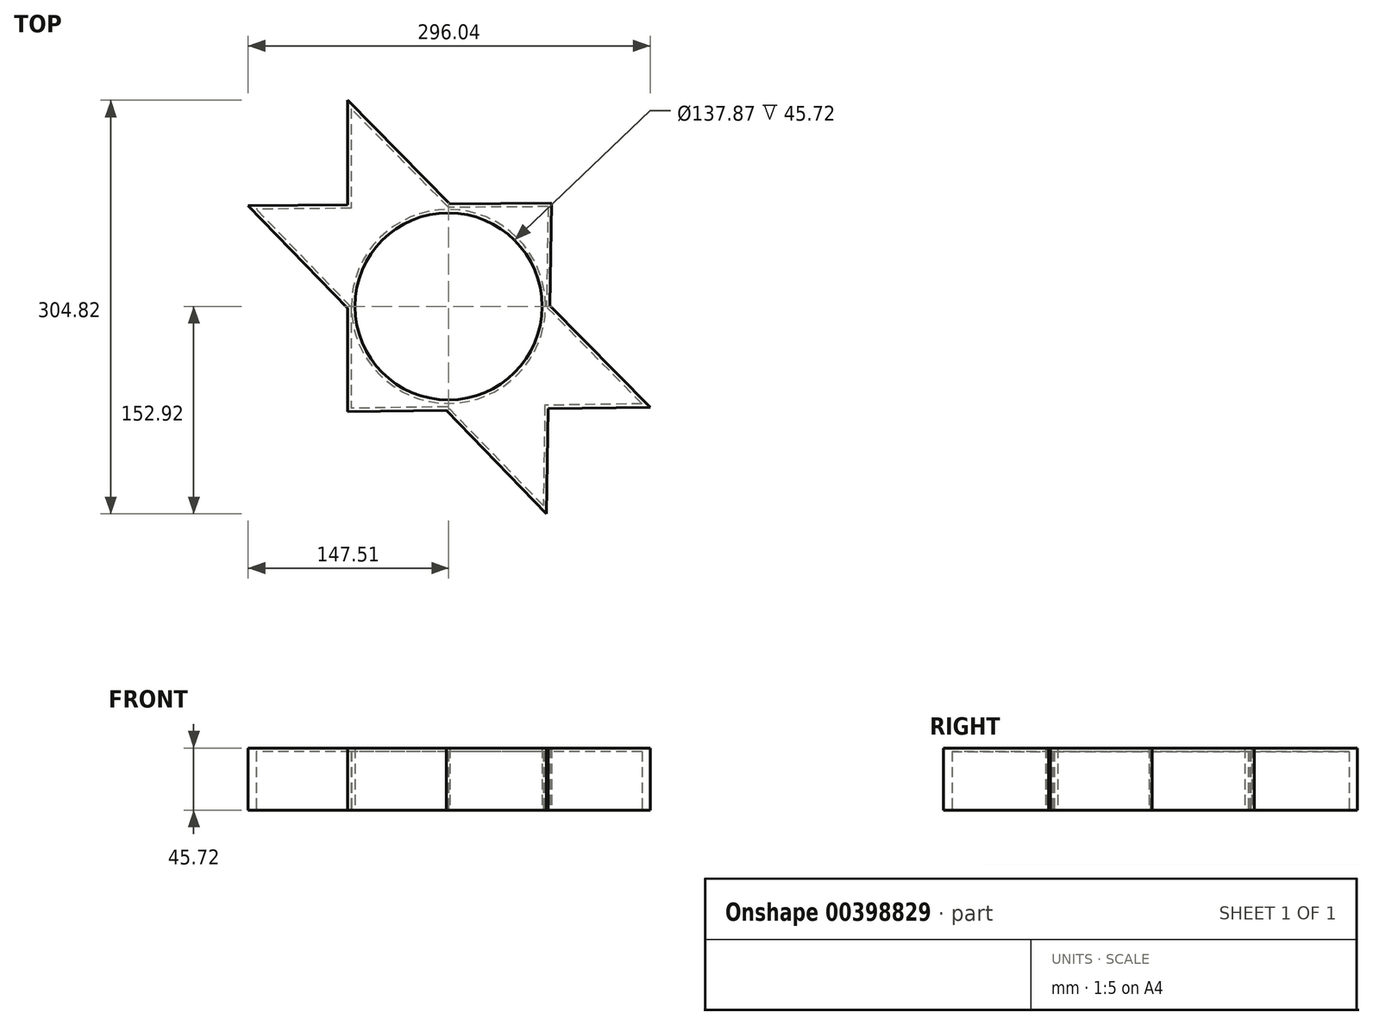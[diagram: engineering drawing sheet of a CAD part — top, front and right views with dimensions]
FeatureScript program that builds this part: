
annotation { "Feature Type Name" : "Feature", "Feature Type Description" : "" }
export const myFeature = defineFeature(function(context is Context, id is Id, definition is map)
    precondition{}
    {
        {
            var Q0;
            Q0=qCreatedBy(makeId("Top.planeOp"),FACE);
            var sketch = newSketch(context, id + "F0", { "sketchPlane" : qUnion([Q0])});
            skLineSegment(sketch, "E0", {"start": v(148.53, -74.26) * mm, "end": v(-74.3, 151.9) * mm});
            skLineSegment(sketch, "E1", {"start": v(-74.3, 151.9) * mm, "end": v(-74.3, -77.7) * mm});
            skLineSegment(sketch, "E2", {"start": v(148.53, -74.26) * mm, "end": v(-74.3, -77.7) * mm});
            skLineSegment(sketch, "E3", {"start": v(75.96, 76.03) * mm, "end": v(72.24, -152.92) * mm});
            skLineSegment(sketch, "E4", {"start": v(72.24, -152.92) * mm, "end": v(-147.51, 74.13) * mm});
            skLineSegment(sketch, "E5", {"start": v(75.96, 76.03) * mm, "end": v(-147.51, 74.13) * mm});
            skCircle(sketch, "E6", {"center": v(0, 0) * mm, "radius": 68.94 * mm});
            skSolve(sketch);
        }
        {
            var Q0;
            Q0 = qSketchRegion(id + "F0", true);
            extrude(context, id + "F1", {"entities" : qUnion([Q0]), "depth" : 45.72 * mm});
        }
        {
            var Q0;
            Q0=makeQuery(id+"F1.opExtrude","CAP_FACE",FACE,{"disambiguationData":[OSD([sQuery(id+"F0.wireOp",EDGE,"E0"),sQuery(id+"F0.wireOp",EDGE,"E1"),sQuery(id+"F0.wireOp",EDGE,"E2"),sQuery(id+"F0.wireOp",EDGE,"E3"),sQuery(id+"F0.wireOp",EDGE,"E4"),sQuery(id+"F0.wireOp",EDGE,"E5")])],"isStart":true});
            shell(context, id + "F2", {"entities" : qUnion([Q0]), "thickness" : 2.54 * mm});
        }
    });
